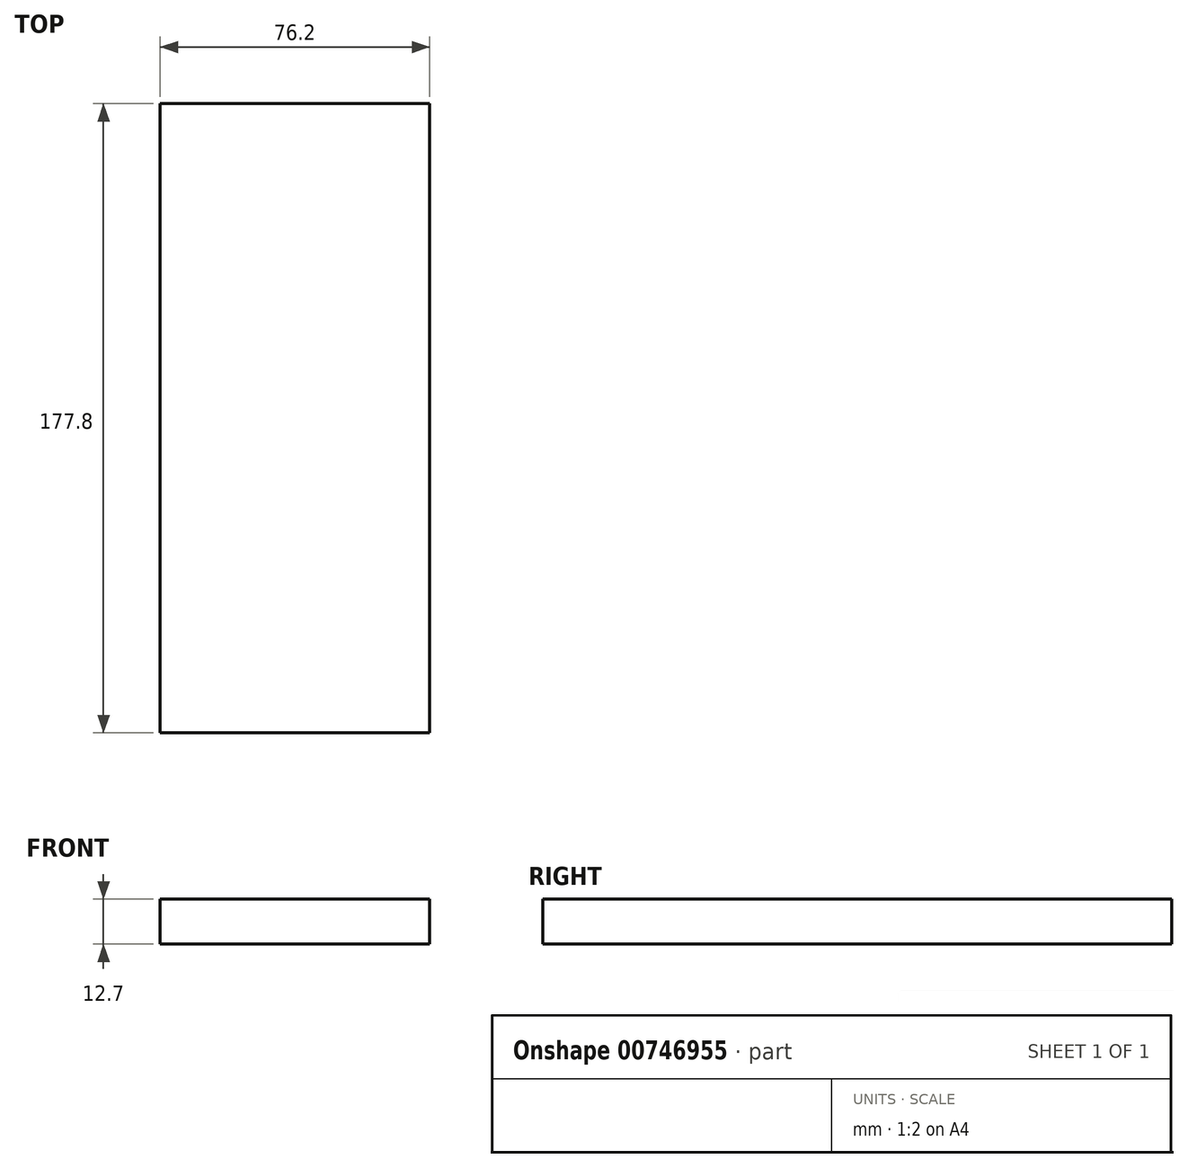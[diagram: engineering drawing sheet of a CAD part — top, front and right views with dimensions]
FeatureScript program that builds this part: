
annotation { "Feature Type Name" : "Feature", "Feature Type Description" : "" }
export const myFeature = defineFeature(function(context is Context, id is Id, definition is map)
    precondition{}
    {
        {
            var Q0;
            Q0=qCreatedBy(makeId("Top.planeOp"),FACE);
            var sketch = newSketch(context, id + "F0", { "sketchPlane" : qUnion([Q0])});
            skLineSegment(sketch, "E0.bottom", {"start": v(38.1, -88.9) * mm, "end": v(-38.1, -88.9) * mm});
            skLineSegment(sketch, "E0.top", {"start": v(38.1, 88.9) * mm, "end": v(-38.1, 88.9) * mm});
            skLineSegment(sketch, "E0.left", {"start": v(38.1, -88.9) * mm, "end": v(38.1, 88.9) * mm});
            skLineSegment(sketch, "E0.right", {"start": v(-38.1, -88.9) * mm, "end": v(-38.1, 88.9) * mm});
            skPoint(sketch, "E0.middle", {"position": v(0, 0) * mm});
            skSolve(sketch);
        }
        {
            var Q0;
            Q0=makeQuery(id+"F0.imprint","IMPRINT",FACE,{"disambiguationData":[TD([[makeQuery(id+"F0.imprint","IMPRINT",EDGE,{"derivedFrom":sQuery(id+"F0.wireOp",EDGE,"E0.bottom")}),-1.0]])]});
            extrude(context, id + "F1", {"entities" : qUnion([Q0]), "depth" : 12.7 * mm, "offsetDistance" : 25.4 * mm});
        }
    });
